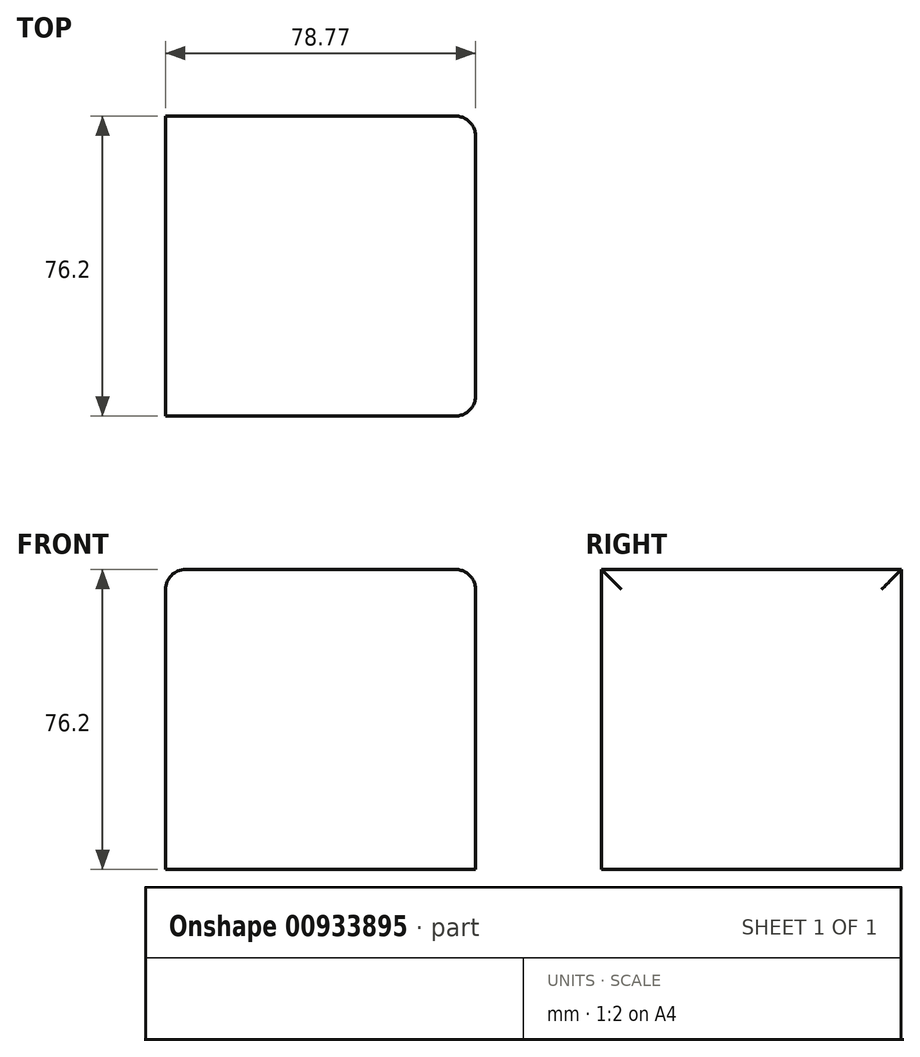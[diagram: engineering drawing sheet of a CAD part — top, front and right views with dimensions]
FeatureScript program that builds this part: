
annotation { "Feature Type Name" : "Feature", "Feature Type Description" : "" }
export const myFeature = defineFeature(function(context is Context, id is Id, definition is map)
    precondition{}
    {
        {
            var Q0;
            Q0=qCreatedBy(makeId("Front.planeOp"),FACE);
            var sketch = newSketch(context, id + "F0", { "sketchPlane" : qUnion([Q0])});
            skLineSegment(sketch, "E0.bottom", {"start": v(-26.26, 26.52) * mm, "end": v(52.51, 26.52) * mm});
            skLineSegment(sketch, "E0.top", {"start": v(-26.26, -49.68) * mm, "end": v(52.51, -49.68) * mm});
            skLineSegment(sketch, "E0.left", {"start": v(-26.26, 26.52) * mm, "end": v(-26.26, -49.68) * mm});
            skLineSegment(sketch, "E0.right", {"start": v(52.51, 26.52) * mm, "end": v(52.51, -49.68) * mm});
            skSolve(sketch);
        }
        {
            var Q0;
            Q0 = qSketchRegion(id + "F0", true);
            extrude(context, id + "F1", {"entities" : qUnion([Q0]), "depth" : 76.2 * mm, "offsetDistance" : 25.4 * mm});
        }
        {
            var Q0;
            Q0=makeQuery(id+"F1.opExtrude","CAP_EDGE",EDGE,{"disambiguationData":[OSD([sQuery(id+"F0.wireOp",EDGE,"E0.right")])],"isStart":false});
            var Q1;
            Q1=makeQuery(id+"F1.opExtrude","SWEPT_EDGE",EDGE,{"disambiguationData":[OSD([sQuery(id+"F0.wireOp",EDGE,"E0.bottom"),sQuery(id+"F0.wireOp",EDGE,"E0.right")])]});
            var Q2;
            Q2=makeQuery(id+"F1.opExtrude","CAP_EDGE",EDGE,{"disambiguationData":[OSD([sQuery(id+"F0.wireOp",EDGE,"E0.right")])],"isStart":true});
            var Q3;
            Q3=makeQuery(id+"F1.opExtrude","SWEPT_EDGE",EDGE,{"disambiguationData":[OSD([sQuery(id+"F0.wireOp",EDGE,"E0.bottom"),sQuery(id+"F0.wireOp",EDGE,"E0.left")])]});
            fillet(context, id + "F2", {"entities" : qUnion([Q0, Q1, Q2, Q3]), "radius" : 5.08 * mm, "tangentPropagation" : true, "allowEdgeOverflow" : false});
        }
    });
